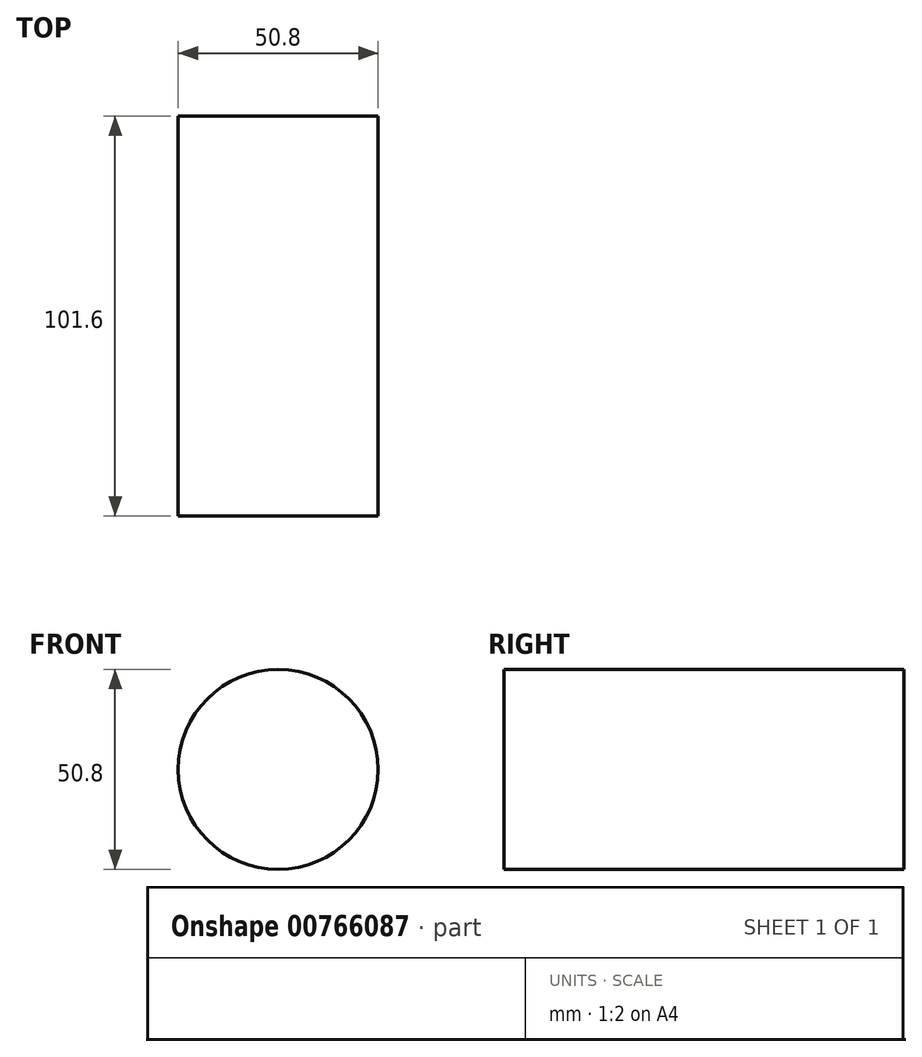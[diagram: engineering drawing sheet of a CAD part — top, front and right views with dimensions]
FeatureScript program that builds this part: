
annotation { "Feature Type Name" : "Feature", "Feature Type Description" : "" }
export const myFeature = defineFeature(function(context is Context, id is Id, definition is map)
    precondition{}
    {
        {
            var Q0;
            Q0=qCreatedBy(makeId("Front.planeOp"),FACE);
            var sketch = newSketch(context, id + "F0", { "sketchPlane" : qUnion([Q0])});
            skEllipse(sketch, "E0", {"center": v(0, 0) * mm, "majorRadius": 25.4 * mm, "minorRadius": 25.4 * mm, "majorAxis": v(1, 0.14)});
            skSolve(sketch);
        }
        {
            var Q0;
            Q0 = qSketchRegion(id + "F0", true);
            extrude(context, id + "F1", {"entities" : qUnion([Q0]), "depth" : 50.8 * mm, "offsetDistance" : 25.4 * mm, "hasSecondDirection" : true, "secondDirectionOppositeDirection" : true, "secondDirectionDepth" : 50.8 * mm});
        }
    });
